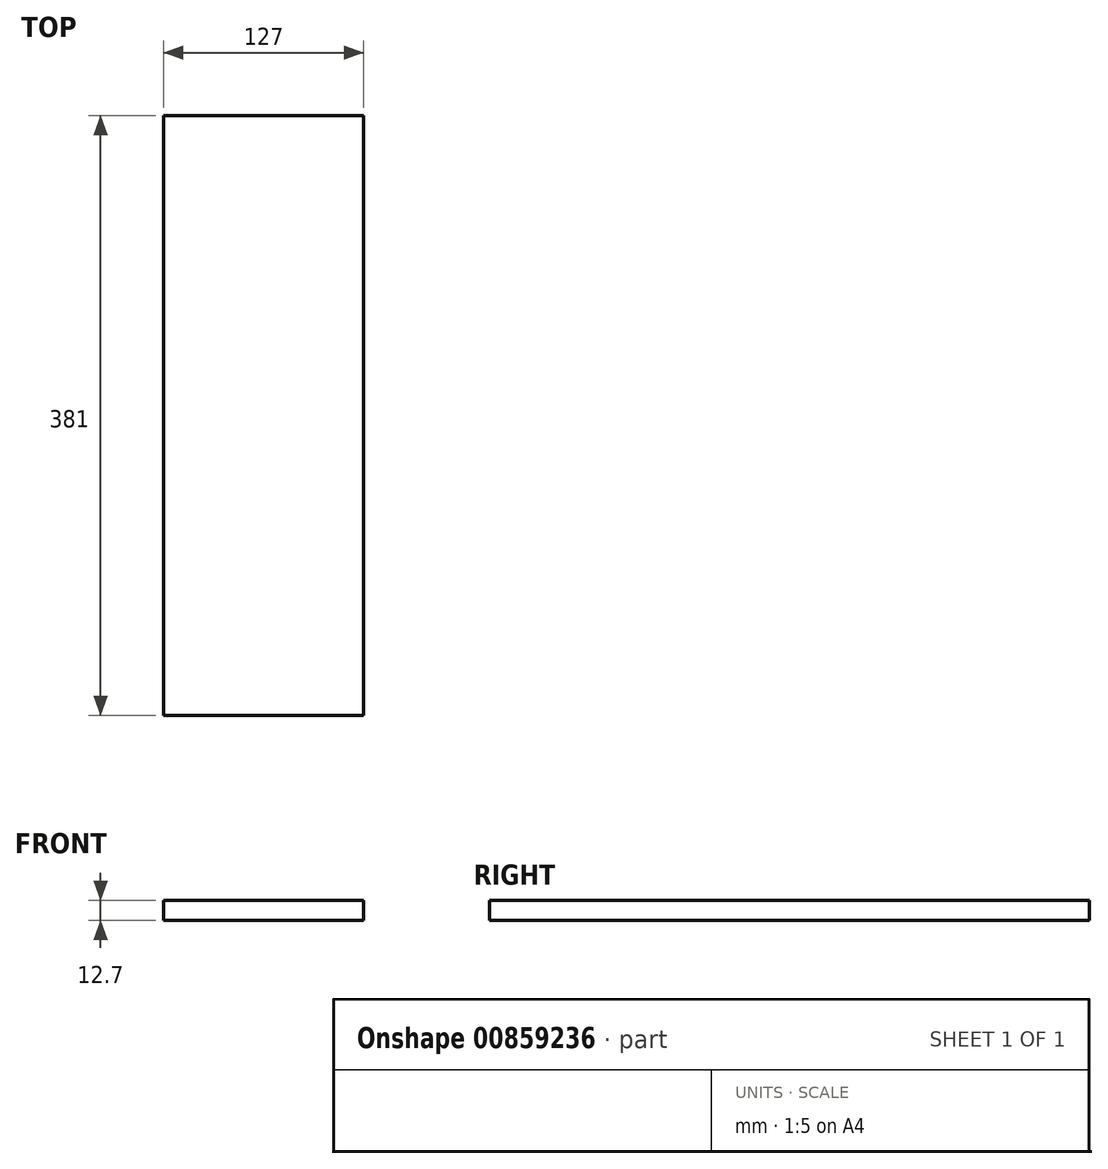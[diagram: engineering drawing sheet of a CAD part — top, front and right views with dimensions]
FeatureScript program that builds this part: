
annotation { "Feature Type Name" : "Feature", "Feature Type Description" : "" }
export const myFeature = defineFeature(function(context is Context, id is Id, definition is map)
    precondition{}
    {
        {
            var Q0;
            Q0=qCreatedBy(makeId("Top.planeOp"),FACE);
            var sketch = newSketch(context, id + "F0", { "sketchPlane" : qUnion([Q0])});
            skLineSegment(sketch, "E0.bottom", {"start": v(0, 0) * mm, "end": v(-127, 0) * mm});
            skLineSegment(sketch, "E0.top", {"start": v(0, 381) * mm, "end": v(-127, 381) * mm});
            skLineSegment(sketch, "E0.left", {"start": v(0, 0) * mm, "end": v(0, 381) * mm});
            skLineSegment(sketch, "E0.right", {"start": v(-127, 0) * mm, "end": v(-127, 381) * mm});
            skSolve(sketch);
        }
        {
            var Q0;
            Q0 = qSketchRegion(id + "F0", true);
            extrude(context, id + "F1", {"entities" : qUnion([Q0]), "depth" : 12.7 * mm, "offsetDistance" : 25.4 * mm});
        }
    });
